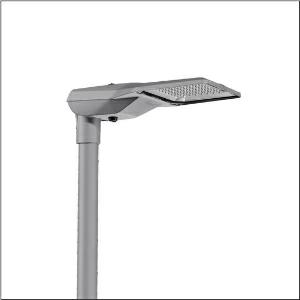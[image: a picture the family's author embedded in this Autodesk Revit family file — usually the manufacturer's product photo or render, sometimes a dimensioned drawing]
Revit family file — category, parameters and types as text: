
# Revit family: streetlight_sl_21_midi___pc-r_5xe3g43t08mb_6611
name_source: partatom
category: Lighting Fixtures
units: mm (PartAtom-declared; Revit-internal decimal feet)

## family parameters
Cut with Voids When Loaded = No
Host = Face
Light Source = No
Part Type = Normal
Room Calculation Point = No
Round Connector Dimension = Use Diameter
Shared = No

## types (1)
- --- (1 x LED, 19200 lm, 147 W, 4000K)
    Apparent Load = 147 VA
    CIE Flux Codes = 38 78 98 100 100
    Color Rendering = 70
    Color Temperature = 4000K
    Default Elevation = 1800 mm
    Description = Streetlight SL 21 midi, mast luminaire, primary light control with lens, of PMMA, primary optical cover: cover, of toughened safety glass, transparent, light distribution: PC-R, light emission: direct distribution, primary light characteristic: asymmetric, right, installation type: side-entry, post-top, LED, High Power LED, rated luminous flux: 19.200lm, luminous efficacy: 131lm/W, light colour: 740, colour temperature: 4000K, control gear: D4i, control: overheat protection, constant luminous flux control, time-dependent luminous flux control, flexible luminous flux parameterisation, pre-setting: logarithmic dimming characteristic, mains connection: 230..240V, AC, 50/60Hz, start of lifetime: 147W, end of service life: 155W, reduction: 65W, luminaire housing, of diecast aluminium, powder-coated, SITECO metallic grey (DB 702S), corrosivity category C5 high according to DIN EN ISO 12944, please order mast flange separately, inclination adjustable: 0°, 5°, 10°, 15°, sealing non-destructively replaceable, multi-level sealing system, length: 644mm, width: 335mm, height: 110mm, mast flange for spigot size: 42mm (side-entry): 5XC10008XM4, 60/48mm (side-entry/post-top): 5XC10108XM2, 76/60mm (side-entry/post-top): 5XC10108XM1, mounting height: 4..8m, Smart Interface below and above, protection rating (complete): IP66, insulation class (complete): insulation class II (safety insulation), certification: CE, ENEC, ENEC+, VDE, impact resistance: IK10, permissible operating ambient temperature for outdoor applications: -40..+50°C, standard-compliant lighting for roads and squares, packaging unit: 1 piece

Light Distribution: PC-R
    Height = 111 mm
    Lamp = 1 x LED
    Lamp Light Flux = 19200 lm
    Lamp Power = 147 W
    Lamp count = 1
    Length = 644 mm
    Luminous efficacy = 131 lm/W
    Manufacturer = Siteco
    ModVariant = No
    Model = 5XE3G43T08MB
    Mounting Place = Pole
    Mounting Type = Pole top
    Number of Poles = 1
    OnlyDefault = Yes
    Power Factor = 1
    Product Name = Streetlight SL 21 midi | PC-R
    Product group = mast luminaire | pylon top
    ProductGroupID = 6100
    Protection Class = Protection class II
    Protection Degree = IP 66
    RLX_Detail_Level = 1
    RLX_Emergency_Light_Flux = 0 lm
    RLX_Emergency_Type = 0
    RLX_Emergency_Type_DB = No
    RlxData = <blob elided: 29517 chars, md5=ce17cd73>
    Socket = socket
    Standby Power = 0 W
    System Light Flux = 19200 lm
    System Power = 147 W
    Type Comments = factory setting: luminous flux: 100 % | dim-lin: 254 | 750 mA
    Type Image = l_1004304.jpg
    URL = http://relux.com
    VarID = @adj_073185
    Voltage = 0 V
    Weight = 0.00 kg
    Width = 336 mm

## geometry (parser evidence)
native form markers: Blend x4, Sweep x10
no freeform markers — native parametric forms only
